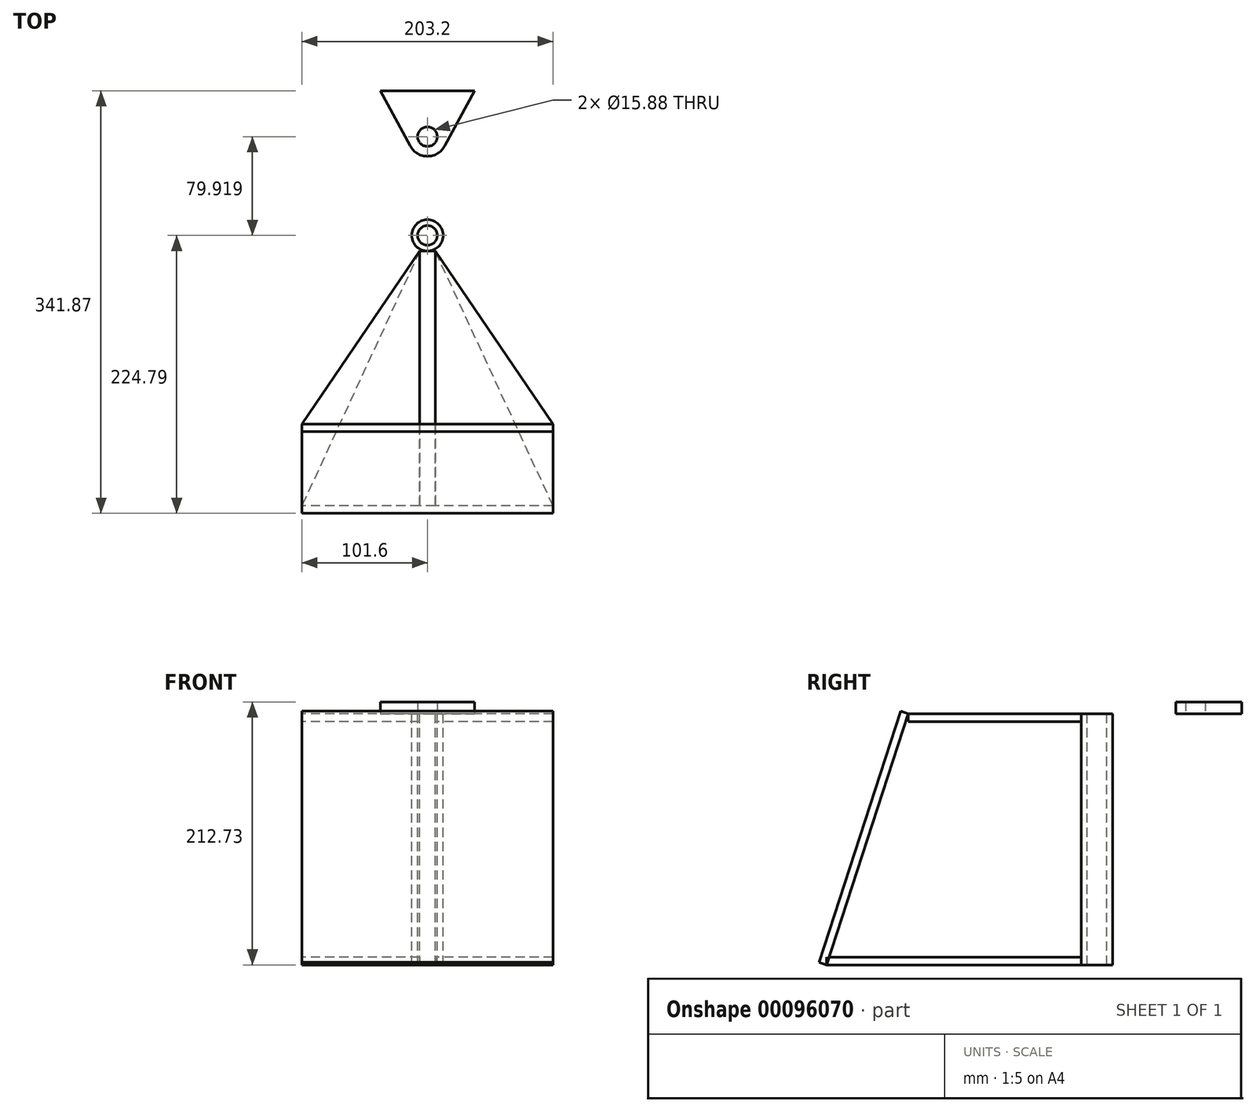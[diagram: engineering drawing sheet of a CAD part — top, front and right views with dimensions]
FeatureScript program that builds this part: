
annotation { "Feature Type Name" : "Feature", "Feature Type Description" : "" }
export const myFeature = defineFeature(function(context is Context, id is Id, definition is map)
    precondition{}
    {
        {
            var Q0;
            Q0=qCreatedBy(makeId("Top.planeOp"),FACE);
            var sketch = newSketch(context, id + "F0", { "sketchPlane" : qUnion([Q0])});
            skCircle(sketch, "E0", {"center": v(0, 0) * mm, "radius": 12.7 * mm});
            skCircle(sketch, "E1", {"center": v(0, 0) * mm, "radius": 7.94 * mm});
            skSolve(sketch);
        }
        {
            var Q0;
            Q0 = qSketchRegion(id + "F0", true);
            extrude(context, id + "F1", {"entities" : qUnion([Q0]), "oppositeDirection" : true, "depth" : 203.2 * mm});
        }
        {
            var Q0;
            Q0=qCreatedBy(makeId("Top.planeOp"),FACE);
            var sketch = newSketch(context, id + "F2", { "sketchPlane" : qUnion([Q0])});
            skPoint(sketch, "E2", {"position": v(0, 79.92) * mm});
            skCircle(sketch, "E3", {"center": v(0, 79.92) * mm, "radius": 15.88 * mm});
            skLineSegment(sketch, "E4", {"start": v(-13.97, 72.38) * mm, "end": v(-38.1, 117.08) * mm});
            skLineSegment(sketch, "E5", {"start": v(-38.1, 117.08) * mm, "end": v(38.1, 117.08) * mm});
            skLineSegment(sketch, "E6", {"start": v(38.1, 117.08) * mm, "end": v(13.97, 72.38) * mm});
            skLineSegment(sketch, "E7", {"start": v(0, 79.92) * mm, "end": v(0, 117.08) * mm, "construction": true});
            skCircle(sketch, "E8", {"center": v(0, 79.92) * mm, "radius": 7.94 * mm});
            skSolve(sketch);
        }
        {
            var Q0;
            Q0 = qSketchRegion(id + "F2", true);
            extrude(context, id + "F3", {"entities" : qUnion([Q0]), "depth" : 9.52 * mm});
        }
        {
            var Q0;
            Q0=qCreatedBy(makeId("Right.planeOp"),FACE);
            var sketch = newSketch(context, id + "F4", { "sketchPlane" : qUnion([Q0])});
            skLineSegment(sketch, "E9.0", {"start": v(-12.7, 0) * mm, "end": v(12.7, 0) * mm});
            skLineSegment(sketch, "E10", {"start": v(-12.7, 0) * mm, "end": v(-14.6, 0) * mm});
            skLineSegment(sketch, "E11", {"start": v(-14.6, 0) * mm, "end": v(-152.73, 0) * mm});
            skLineSegment(sketch, "E12", {"start": v(-152.73, 0) * mm, "end": v(-218.75, -203.2) * mm});
            skLineSegment(sketch, "E13.0", {"start": v(-12.7, -203.2) * mm, "end": v(12.7, -203.2) * mm});
            skLineSegment(sketch, "E14", {"start": v(-218.75, -203.2) * mm, "end": v(-12.7, -203.2) * mm});
            skLineSegment(sketch, "E15", {"start": v(-12.7, -203.2) * mm, "end": v(-12.7, 0) * mm});
            skSolve(sketch);
        }
        {
            var Q0;
            Q0 = qSketchRegion(id + "F4", true);
            extrude(context, id + "F5", {"entities" : qUnion([Q0]), "operationType" : NewBodyOperationType.ADD, "endBound" : BoundingType.SYMMETRIC, "depth" : 12.7 * mm});
        }
        {
            var Q0;
            Q0=makeQuery(id+"F5.opExtrude","SWEPT_FACE",FACE,{"disambiguationData":[OSD([sQuery(id+"F4.wireOp",EDGE,"E12")])]});
            var sketch = newSketch(context, id + "F6", { "sketchPlane" : qUnion([Q0])});
            skLineSegment(sketch, "E16.0", {"start": v(6.35, -47.2) * mm, "end": v(-6.35, -47.2) * mm});
            skLineSegment(sketch, "E17.0", {"start": v(6.35, -260.85) * mm, "end": v(-6.35, -260.85) * mm});
            skLineSegment(sketch, "E18.bottom", {"start": v(-101.6, -47.2) * mm, "end": v(101.6, -47.2) * mm});
            skLineSegment(sketch, "E18.top", {"start": v(-101.6, -260.85) * mm, "end": v(101.6, -260.85) * mm});
            skLineSegment(sketch, "E18.left", {"start": v(-101.6, -47.2) * mm, "end": v(-101.6, -260.85) * mm});
            skLineSegment(sketch, "E18.right", {"start": v(101.6, -47.2) * mm, "end": v(101.6, -260.85) * mm});
            skSolve(sketch);
        }
        {
            var Q0;
            {var subQ1=sQuery(id+"F4.wireOp",EDGE,"E12");var subQ2=makeQuery(id+"F5.opExtrude","CAP_EDGE",EDGE,{"disambiguationData":[OSD([subQ1])],"isStart":true});Q0=makeQuery(id+"F6.imprint","IMPRINT",FACE,{"disambiguationData":[TD([[makeQuery(id+"F6.imprint","IMPRINT",EDGE,{"derivedFrom":subQ2}),1.0]])]});}
            var Q1;
            {var subQ2=sQuery(id+"F6.wireOp",EDGE,"E18.right");Q1=makeQuery(id+"F6.imprint","IMPRINT",FACE,{"disambiguationData":[TD([[makeQuery(id+"F6.imprint","IMPRINT",EDGE,{"derivedFrom":subQ2}),-1.0]])]});}
            var Q2;
            {var subQ2=sQuery(id+"F6.wireOp",EDGE,"E18.left");Q2=makeQuery(id+"F6.imprint","IMPRINT",FACE,{"disambiguationData":[TD([[makeQuery(id+"F6.imprint","IMPRINT",EDGE,{"derivedFrom":subQ2}),1.0]])]});}
            extrude(context, id + "F7", {"entities" : qUnion([Q0, Q1, Q2]), "operationType" : NewBodyOperationType.ADD, "depth" : 6.35 * mm});
        }
        {
            var Q0;
            Q0=makeQuery(id+"F5.opExtrude","SWEPT_FACE",FACE,{"disambiguationData":[OSD([sQuery(id+"F4.wireOp",EDGE,"E14")])]});
            cPlane(context, id + "F8", {"entities" : qUnion([Q0]), "cplaneType" : CPlaneType.OFFSET, "offset" : 0 * mm, "width" : 152.4 * mm, "height" : 152.4 * mm});
        }
        {
            var Q0;
            Q0=qCreatedBy(id+"F8.planeOp",FACE);
            var sketch = newSketch(context, id + "F9", { "sketchPlane" : qUnion([Q0])});
            skPoint(sketch, "E19.0", {"position": v(101.6, 218.75) * mm});
            skPoint(sketch, "E20.0", {"position": v(6.35, 218.75) * mm});
            skPoint(sketch, "E21.0", {"position": v(-6.35, 218.75) * mm});
            skPoint(sketch, "E22.0", {"position": v(-101.6, 218.75) * mm});
            skLineSegment(sketch, "E23.0", {"start": v(-6.35, 218.75) * mm, "end": v(-101.6, 218.75) * mm});
            skLineSegment(sketch, "E24.0", {"start": v(101.6, 218.75) * mm, "end": v(6.35, 218.75) * mm});
            skLineSegment(sketch, "E25.0", {"start": v(6.35, 218.75) * mm, "end": v(6.35, 12.7) * mm});
            skLineSegment(sketch, "E26.0", {"start": v(-6.35, 218.75) * mm, "end": v(-6.35, 12.7) * mm});
            skLineSegment(sketch, "E27", {"start": v(101.6, 218.75) * mm, "end": v(6.35, 12.7) * mm});
            skLineSegment(sketch, "E28", {"start": v(-6.35, 12.7) * mm, "end": v(-101.6, 218.75) * mm});
            skSolve(sketch);
        }
        {
            var Q0;
            Q0=qCreatedBy(makeId("Top.planeOp"),FACE);
            var sketch = newSketch(context, id + "F10", { "sketchPlane" : qUnion([Q0])});
            skLineSegment(sketch, "E29.0", {"start": v(6.35, -12.7) * mm, "end": v(6.35, -152.73) * mm});
            skLineSegment(sketch, "E30.0", {"start": v(101.6, -152.73) * mm, "end": v(6.35, -152.73) * mm});
            skLineSegment(sketch, "E31", {"start": v(101.6, -152.73) * mm, "end": v(6.35, -12.7) * mm});
            skPoint(sketch, "E32.0", {"position": v(-101.6, -152.73) * mm});
            skPoint(sketch, "E33.0", {"position": v(-6.35, -12.7) * mm});
            skLineSegment(sketch, "E34", {"start": v(-6.35, -12.7) * mm, "end": v(-101.6, -152.73) * mm});
            skLineSegment(sketch, "E35.0", {"start": v(-6.35, -152.73) * mm, "end": v(-101.6, -152.73) * mm});
            skLineSegment(sketch, "E36.0", {"start": v(-6.35, -12.7) * mm, "end": v(-6.35, -152.73) * mm});
            skSolve(sketch);
        }
        {
            var Q0;
            Q0=makeQuery(id+"F10.imprint","IMPRINT",FACE,{"disambiguationData":[TD([[makeQuery(id+"F10.imprint","IMPRINT",EDGE,{"derivedFrom":sQuery(id+"F10.wireOp",EDGE,"E34")}),1.0]])]});
            var Q1;
            Q1=makeQuery(id+"F10.imprint","IMPRINT",FACE,{"disambiguationData":[TD([[makeQuery(id+"F10.imprint","IMPRINT",EDGE,{"derivedFrom":sQuery(id+"F10.wireOp",EDGE,"E29.0")}),1.0]])]});
            extrude(context, id + "F11", {"entities" : qUnion([Q0, Q1]), "oppositeDirection" : true, "depth" : 6.35 * mm});
        }
        {
            var Q0;
            Q0=makeQuery(id+"F9.imprint","IMPRINT",FACE,{"disambiguationData":[TD([[makeQuery(id+"F9.imprint","IMPRINT",EDGE,{"derivedFrom":sQuery(id+"F9.wireOp",EDGE,"E23.0")}),1.0]])]});
            var Q1;
            Q1=makeQuery(id+"F9.imprint","IMPRINT",FACE,{"disambiguationData":[TD([[makeQuery(id+"F9.imprint","IMPRINT",EDGE,{"derivedFrom":sQuery(id+"F9.wireOp",EDGE,"E24.0")}),1.0]])]});
            extrude(context, id + "F12", {"entities" : qUnion([Q0, Q1]), "oppositeDirection" : true, "depth" : 6.35 * mm});
        }
    });
